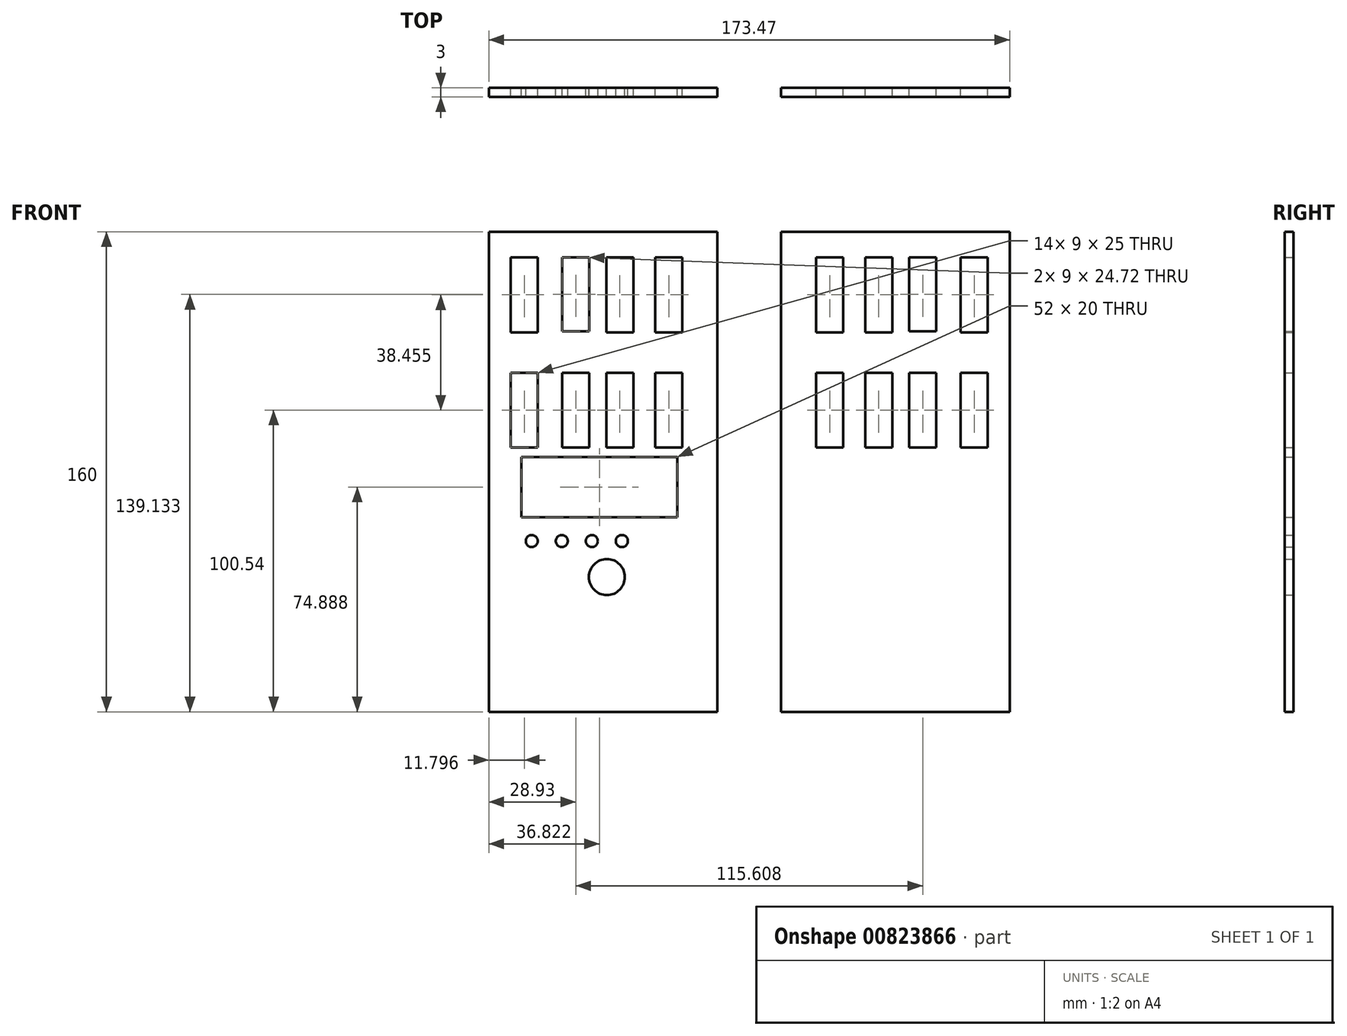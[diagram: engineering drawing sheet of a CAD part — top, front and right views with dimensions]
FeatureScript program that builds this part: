
annotation { "Feature Type Name" : "Feature", "Feature Type Description" : "" }
export const myFeature = defineFeature(function(context is Context, id is Id, definition is map)
    precondition{}
    {
        {
            var Q0;
            Q0=qCreatedBy(makeId("Front.planeOp"),FACE);
            var sketch = newSketch(context, id + "F0", { "sketchPlane" : qUnion([Q0])});
            skLineSegment(sketch, "E0", {"start": v(-33.43, -116.74) * mm, "end": v(-33.43, 43.26) * mm});
            skLineSegment(sketch, "E1", {"start": v(42.69, -116.74) * mm, "end": v(42.69, 43.26) * mm});
            skLineSegment(sketch, "E2", {"start": v(-26.13, 34.76) * mm, "end": v(-26.13, 9.76) * mm});
            skLineSegment(sketch, "E3", {"start": v(-26.13, 9.76) * mm, "end": v(-17.13, 9.76) * mm});
            skLineSegment(sketch, "E4", {"start": v(-17.13, 9.76) * mm, "end": v(-17.13, 34.76) * mm});
            skLineSegment(sketch, "E5", {"start": v(-17.13, 34.76) * mm, "end": v(-26.13, 34.76) * mm});
            skLineSegment(sketch, "E6", {"start": v(-9, 34.76) * mm, "end": v(-9, 10.03) * mm});
            skLineSegment(sketch, "E7", {"start": v(-9, 10.03) * mm, "end": v(0, 10.03) * mm});
            skLineSegment(sketch, "E8", {"start": v(0, 10.03) * mm, "end": v(0, 34.76) * mm});
            skLineSegment(sketch, "E9", {"start": v(0, 34.76) * mm, "end": v(-9, 34.76) * mm});
            skLineSegment(sketch, "E10", {"start": v(5.7, 9.76) * mm, "end": v(5.7, 34.76) * mm});
            skLineSegment(sketch, "E11", {"start": v(5.7, 9.76) * mm, "end": v(14.7, 9.76) * mm});
            skLineSegment(sketch, "E12", {"start": v(14.7, 9.76) * mm, "end": v(14.7, 34.76) * mm});
            skLineSegment(sketch, "E13", {"start": v(14.7, 34.76) * mm, "end": v(5.7, 34.76) * mm});
            skLineSegment(sketch, "E14", {"start": v(22.01, 9.76) * mm, "end": v(22.01, 34.76) * mm});
            skLineSegment(sketch, "E15", {"start": v(22.01, 34.76) * mm, "end": v(31.01, 34.76) * mm});
            skLineSegment(sketch, "E16", {"start": v(31.01, 34.76) * mm, "end": v(31.01, 9.76) * mm});
            skLineSegment(sketch, "E17", {"start": v(31.01, 9.76) * mm, "end": v(22.01, 9.76) * mm});
            skLineSegment(sketch, "E18", {"start": v(12.87, -116.74) * mm, "end": v(12.87, -89.01) * mm});
            skLineSegment(sketch, "E19", {"start": v(12.87, -116.74) * mm, "end": v(27.87, -116.74) * mm});
            skLineSegment(sketch, "E20", {"start": v(27.87, -116.74) * mm, "end": v(27.87, -89.01) * mm});
            skLineSegment(sketch, "E21", {"start": v(27.87, -89.01) * mm, "end": v(22.1, -74.53) * mm});
            skLineSegment(sketch, "E22", {"start": v(42.69, 43.26) * mm, "end": v(-33.43, 43.26) * mm});
            skLineSegment(sketch, "E23", {"start": v(0, -12.1) * mm, "end": v(0, 22.4) * mm});
            skLineSegment(sketch, "E24", {"start": v(-26.13, -3.7) * mm, "end": v(-26.13, -28.7) * mm});
            skLineSegment(sketch, "E25", {"start": v(-26.13, -28.7) * mm, "end": v(-17.13, -28.7) * mm});
            skLineSegment(sketch, "E26", {"start": v(-17.13, -28.7) * mm, "end": v(-17.13, -3.7) * mm});
            skLineSegment(sketch, "E27", {"start": v(-17.13, -3.7) * mm, "end": v(-26.13, -3.7) * mm});
            skLineSegment(sketch, "E28", {"start": v(-9, -3.7) * mm, "end": v(-9, -28.7) * mm});
            skLineSegment(sketch, "E29", {"start": v(-9, -28.7) * mm, "end": v(0, -28.7) * mm});
            skLineSegment(sketch, "E30", {"start": v(0, -28.7) * mm, "end": v(0, -3.7) * mm});
            skLineSegment(sketch, "E31", {"start": v(0, -3.7) * mm, "end": v(-9, -3.7) * mm});
            skLineSegment(sketch, "E32", {"start": v(5.7, -3.7) * mm, "end": v(5.7, -28.7) * mm});
            skLineSegment(sketch, "E33", {"start": v(5.7, -28.7) * mm, "end": v(14.7, -28.7) * mm});
            skLineSegment(sketch, "E34", {"start": v(14.7, -28.7) * mm, "end": v(14.7, -3.7) * mm});
            skLineSegment(sketch, "E35", {"start": v(14.7, -3.7) * mm, "end": v(5.7, -3.7) * mm});
            skLineSegment(sketch, "E36", {"start": v(22.01, -3.7) * mm, "end": v(22.01, -28.7) * mm});
            skLineSegment(sketch, "E37", {"start": v(22.01, -28.7) * mm, "end": v(31.01, -28.7) * mm});
            skLineSegment(sketch, "E38", {"start": v(31.01, -28.7) * mm, "end": v(31.01, -3.7) * mm});
            skLineSegment(sketch, "E39", {"start": v(31.01, -3.7) * mm, "end": v(22.01, -3.7) * mm});
            skLineSegment(sketch, "E40", {"start": v(-33.43, 34.76) * mm, "end": v(-33.43, -90.2) * mm});
            skLineSegment(sketch, "E41", {"start": v(-33.43, -116.74) * mm, "end": v(27.87, -116.74) * mm});
            skLineSegment(sketch, "E42", {"start": v(-20.36, -116.74) * mm, "end": v(-5.36, -116.74) * mm});
            skLineSegment(sketch, "E43", {"start": v(-20.36, -116.74) * mm, "end": v(-20.36, -88.74) * mm});
            skLineSegment(sketch, "E44", {"start": v(-5.36, -116.74) * mm, "end": v(-5.36, -88.74) * mm});
            skLineSegment(sketch, "E45", {"start": v(-20.36, -88.74) * mm, "end": v(-15.25, -74.63) * mm});
            skLineSegment(sketch, "E46", {"start": v(-5.36, -88.74) * mm, "end": v(-10.7, -74.72) * mm});
            skArc(sketch, "E47", {"start": v(-10.7, -74.72) * mm, "mid": v(-12.88, -69.32) * mm, "end": v(-15.25, -74.63) * mm});
            skLineSegment(sketch, "E48", {"start": v(12.87, -89.01) * mm, "end": v(16.94, -74.58) * mm});
            skArc(sketch, "E49", {"start": v(22.1, -74.53) * mm, "mid": v(19.47, -69.57) * mm, "end": v(16.94, -74.58) * mm});
            skLineSegment(sketch, "E50", {"start": v(42.69, -116.74) * mm, "end": v(26.42, -116.74) * mm});
            skArc(sketch, "E51.MirrorCS", {"start": v(84.5, -74.53) * mm, "mid": v(87.14, -69.57) * mm, "end": v(89.67, -74.58) * mm});
            skLineSegment(sketch, "E52.MirrorCS", {"start": v(123.74, -3.7) * mm, "end": v(132.74, -3.7) * mm});
            skLineSegment(sketch, "E53.MirrorCS", {"start": v(106.6, 34.76) * mm, "end": v(115.6, 34.76) * mm});
            skLineSegment(sketch, "E54.MirrorCS", {"start": v(126.97, -88.74) * mm, "end": v(121.86, -74.63) * mm});
            skLineSegment(sketch, "E55.MirrorCS", {"start": v(100.92, 9.76) * mm, "end": v(100.92, 34.76) * mm});
            skLineSegment(sketch, "E56.MirrorCS", {"start": v(123.74, 34.76) * mm, "end": v(132.74, 34.76) * mm});
            skArc(sketch, "E57.MirrorCS", {"start": v(117.31, -74.72) * mm, "mid": v(119.48, -69.32) * mm, "end": v(121.86, -74.63) * mm});
            skLineSegment(sketch, "E58.MirrorCS", {"start": v(91.92, 34.76) * mm, "end": v(100.92, 34.76) * mm});
            skLineSegment(sketch, "E59.MirrorCS", {"start": v(111.97, -88.74) * mm, "end": v(117.31, -74.72) * mm});
            skLineSegment(sketch, "E60.MirrorCS", {"start": v(132.74, 34.76) * mm, "end": v(132.74, 9.76) * mm});
            skLineSegment(sketch, "E61.MirrorCS", {"start": v(100.92, -28.7) * mm, "end": v(91.92, -28.7) * mm});
            skLineSegment(sketch, "E62.MirrorCS", {"start": v(106.6, 10.03) * mm, "end": v(106.6, 34.76) * mm});
            skLineSegment(sketch, "E63.MirrorCS", {"start": v(91.92, 9.76) * mm, "end": v(91.92, 34.76) * mm});
            skLineSegment(sketch, "E64.MirrorCS", {"start": v(115.6, -28.7) * mm, "end": v(106.6, -28.7) * mm});
            skLineSegment(sketch, "E65.MirrorCS", {"start": v(75.6, 34.76) * mm, "end": v(75.6, 9.76) * mm});
            skLineSegment(sketch, "E66.MirrorCS", {"start": v(93.74, -116.74) * mm, "end": v(78.74, -116.74) * mm});
            skLineSegment(sketch, "E67.MirrorCS", {"start": v(84.6, -28.7) * mm, "end": v(75.6, -28.7) * mm});
            skLineSegment(sketch, "E68.MirrorCS", {"start": v(115.6, 10.03) * mm, "end": v(106.6, 10.03) * mm});
            skLineSegment(sketch, "E69.MirrorCS", {"start": v(100.92, 9.76) * mm, "end": v(91.92, 9.76) * mm});
            skLineSegment(sketch, "E70.MirrorCS", {"start": v(63.92, -116.74) * mm, "end": v(80.2, -116.74) * mm});
            skLineSegment(sketch, "E71.MirrorCS", {"start": v(123.74, 9.76) * mm, "end": v(123.74, 34.76) * mm});
            skLineSegment(sketch, "E72.MirrorCS", {"start": v(91.92, -3.7) * mm, "end": v(100.92, -3.7) * mm});
            skLineSegment(sketch, "E73.MirrorCS", {"start": v(126.97, -116.74) * mm, "end": v(111.97, -116.74) * mm});
            skLineSegment(sketch, "E74.MirrorCS", {"start": v(132.74, -28.7) * mm, "end": v(123.74, -28.7) * mm});
            skLineSegment(sketch, "E75.MirrorCS", {"start": v(84.6, 9.76) * mm, "end": v(84.6, 34.76) * mm});
            skLineSegment(sketch, "E76.MirrorCS", {"start": v(93.74, -89.01) * mm, "end": v(89.67, -74.58) * mm});
            skLineSegment(sketch, "E77.MirrorCS", {"start": v(78.74, -89.01) * mm, "end": v(84.5, -74.53) * mm});
            skLineSegment(sketch, "E78.MirrorCS", {"start": v(106.6, -3.7) * mm, "end": v(115.6, -3.7) * mm});
            skLineSegment(sketch, "E79.MirrorCS", {"start": v(75.6, -3.7) * mm, "end": v(84.6, -3.7) * mm});
            skLineSegment(sketch, "E80.MirrorCS", {"start": v(115.6, 34.76) * mm, "end": v(115.6, 10.03) * mm});
            skLineSegment(sketch, "E81.MirrorCS", {"start": v(75.6, 9.76) * mm, "end": v(84.6, 9.76) * mm});
            skLineSegment(sketch, "E82.MirrorCS", {"start": v(132.74, 9.76) * mm, "end": v(123.74, 9.76) * mm});
            skLineSegment(sketch, "E83.MirrorCS", {"start": v(140.04, -116.74) * mm, "end": v(78.74, -116.74) * mm});
            skLineSegment(sketch, "E84.MirrorCS", {"start": v(84.6, 34.76) * mm, "end": v(75.6, 34.76) * mm});
            skLineSegment(sketch, "E85.MirrorCS", {"start": v(91.92, -28.7) * mm, "end": v(91.92, -3.7) * mm});
            skLineSegment(sketch, "E86.MirrorCS", {"start": v(100.92, -3.7) * mm, "end": v(100.92, -28.7) * mm});
            skLineSegment(sketch, "E87.MirrorCS", {"start": v(84.6, -3.7) * mm, "end": v(84.6, -28.7) * mm});
            skLineSegment(sketch, "E88.MirrorCS", {"start": v(115.6, -3.7) * mm, "end": v(115.6, -28.7) * mm});
            skLineSegment(sketch, "E89.MirrorCS", {"start": v(126.97, -116.74) * mm, "end": v(126.97, -88.74) * mm});
            skLineSegment(sketch, "E90.MirrorCS", {"start": v(123.74, -28.7) * mm, "end": v(123.74, -3.7) * mm});
            skLineSegment(sketch, "E91.MirrorCS", {"start": v(111.97, -116.74) * mm, "end": v(111.97, -88.74) * mm});
            skLineSegment(sketch, "E92.MirrorCS", {"start": v(140.04, 34.76) * mm, "end": v(140.04, -90.2) * mm});
            skLineSegment(sketch, "E93.MirrorCS", {"start": v(132.74, -3.7) * mm, "end": v(132.74, -28.7) * mm});
            skLineSegment(sketch, "E94.MirrorCS", {"start": v(106.6, -28.7) * mm, "end": v(106.6, -3.7) * mm});
            skLineSegment(sketch, "E95.MirrorCS", {"start": v(75.6, -28.7) * mm, "end": v(75.6, -3.7) * mm});
            skLineSegment(sketch, "E96.MirrorCS", {"start": v(93.74, -116.74) * mm, "end": v(93.74, -89.01) * mm});
            skLineSegment(sketch, "E97.MirrorCS", {"start": v(78.74, -116.74) * mm, "end": v(78.74, -89.01) * mm});
            skLineSegment(sketch, "E98.MirrorCS", {"start": v(63.92, -116.74) * mm, "end": v(63.92, 43.26) * mm});
            skLineSegment(sketch, "E99.MirrorCS", {"start": v(140.04, -116.74) * mm, "end": v(140.04, 43.26) * mm});
            skLineSegment(sketch, "E100.MirrorCS", {"start": v(63.92, 43.26) * mm, "end": v(140.04, 43.26) * mm});
            skLineSegment(sketch, "E101.bottom", {"start": v(-22.6, -31.85) * mm, "end": v(29.4, -31.85) * mm});
            skLineSegment(sketch, "E101.top", {"start": v(-22.6, -51.85) * mm, "end": v(29.4, -51.85) * mm});
            skLineSegment(sketch, "E101.left", {"start": v(-22.6, -31.85) * mm, "end": v(-22.6, -51.85) * mm});
            skLineSegment(sketch, "E101.right", {"start": v(29.4, -31.85) * mm, "end": v(29.4, -51.85) * mm});
            skCircle(sketch, "E102", {"center": v(-19.13, -59.82) * mm, "radius": 2 * mm});
            skLineSegment(sketch, "E103", {"start": v(-19.13, -59.82) * mm, "end": v(-9.13, -59.82) * mm});
            skCircle(sketch, "E104", {"center": v(-9.13, -59.82) * mm, "radius": 2 * mm});
            skCircle(sketch, "E105", {"center": v(0.87, -59.82) * mm, "radius": 2 * mm});
            skCircle(sketch, "E106", {"center": v(10.87, -59.82) * mm, "radius": 2 * mm});
            skCircle(sketch, "E107", {"center": v(5.87, -71.82) * mm, "radius": 6 * mm});
            skSolve(sketch);
        }
        {
            var Q0;
            Q0 = qSketchRegion(id + "F0", true);
            extrude(context, id + "F1", {"entities" : qUnion([Q0]), "depth" : 3 * mm, "offsetDistance" : 25 * mm});
        }
    });
